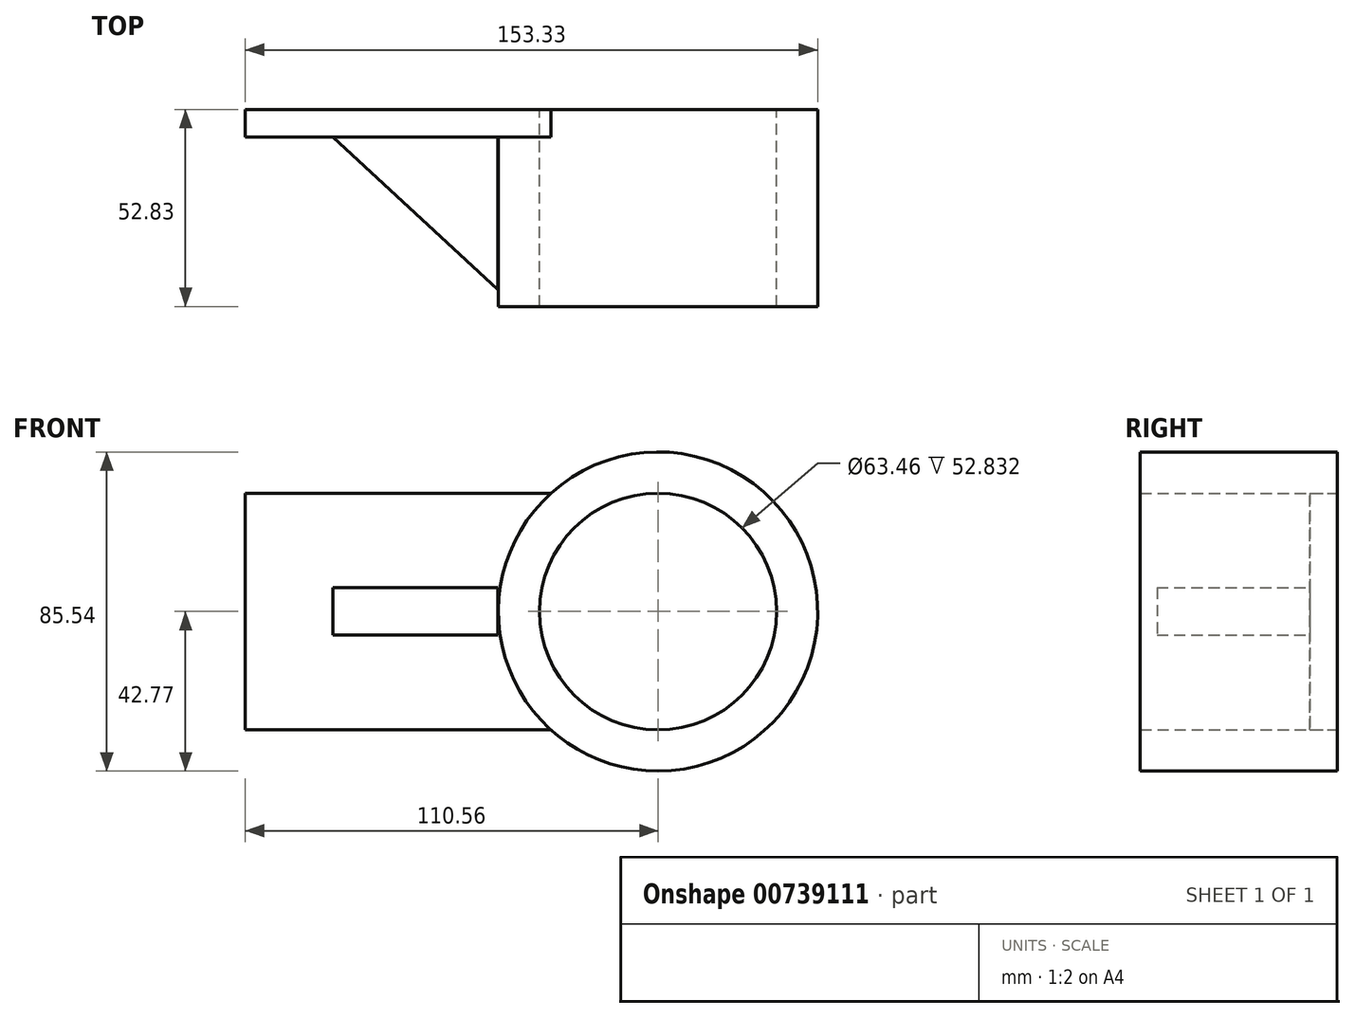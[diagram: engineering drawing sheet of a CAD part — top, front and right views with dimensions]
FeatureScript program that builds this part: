
annotation { "Feature Type Name" : "Feature", "Feature Type Description" : "" }
export const myFeature = defineFeature(function(context is Context, id is Id, definition is map)
    precondition{}
    {
        {
            var Q0;
            Q0=qCreatedBy(makeId("Front.planeOp"),FACE);
            var sketch = newSketch(context, id + "F0", { "sketchPlane" : qUnion([Q0])});
            skLineSegment(sketch, "E0.bottom", {"start": v(14.45, -31.74) * mm, "end": v(-67.6, -31.74) * mm});
            skLineSegment(sketch, "E0.top", {"start": v(14.45, 31.74) * mm, "end": v(-67.6, 31.74) * mm});
            skLineSegment(sketch, "E0.right", {"start": v(-67.6, -31.74) * mm, "end": v(-67.6, 31.74) * mm});
            skPoint(sketch, "E0.middle", {"position": v(-26.58, 0) * mm});
            skCircle(sketch, "E1", {"center": v(42.96, 0) * mm, "radius": 42.77 * mm});
            skCircle(sketch, "E2", {"center": v(42.96, 0) * mm, "radius": 31.73 * mm});
            skSolve(sketch);
        }
        {
            var Q0;
            Q0=makeQuery(id+"F0.imprint","IMPRINT",FACE,{"disambiguationData":[TD([[makeQuery(id+"F0.imprint","IMPRINT",EDGE,{"derivedFrom":sQuery(id+"F0.wireOp",EDGE,"E2")}),-1.0]])]});
            extrude(context, id + "F1", {"entities" : qUnion([Q0]), "depth" : 52.83 * mm, "offsetDistance" : 25.4 * mm});
        }
        {
            var Q0;
            {var subQ0=sQuery(id+"F0.wireOp",EDGE,"E0.right");Q0=makeQuery(id+"F0.imprint","IMPRINT",FACE,{"disambiguationData":[TD([[makeQuery(id+"F0.imprint","IMPRINT",EDGE,{"derivedFrom":subQ0}),-1.0]])]});}
            extrude(context, id + "F2", {"entities" : qUnion([Q0]), "operationType" : NewBodyOperationType.ADD, "depth" : 7.37 * mm, "offsetDistance" : 25.4 * mm});
        }
        {
            var Q0;
            Q0=qCreatedBy(makeId("Top.planeOp"),FACE);
            var sketch = newSketch(context, id + "F3", { "sketchPlane" : qUnion([Q0])});
            skLineSegment(sketch, "E3", {"start": v(-44.12, -7.4) * mm, "end": v(0, -7.4) * mm});
            skLineSegment(sketch, "E4", {"start": v(0, -7.4) * mm, "end": v(0, -48.35) * mm});
            skLineSegment(sketch, "E5", {"start": v(0, -48.35) * mm, "end": v(-44.12, -7.4) * mm});
            skSolve(sketch);
        }
        {
            var Q0;
            Q0=makeQuery(id+"F3.imprint","IMPRINT",FACE,{"disambiguationData":[TD([[makeQuery(id+"F3.imprint","IMPRINT",EDGE,{"derivedFrom":sQuery(id+"F3.wireOp",EDGE,"E3")}),-1.0]])]});
            extrude(context, id + "F4", {"entities" : qUnion([Q0]), "endBound" : BoundingType.SYMMETRIC, "depth" : 12.7 * mm, "offsetDistance" : 25.4 * mm});
        }
    });
